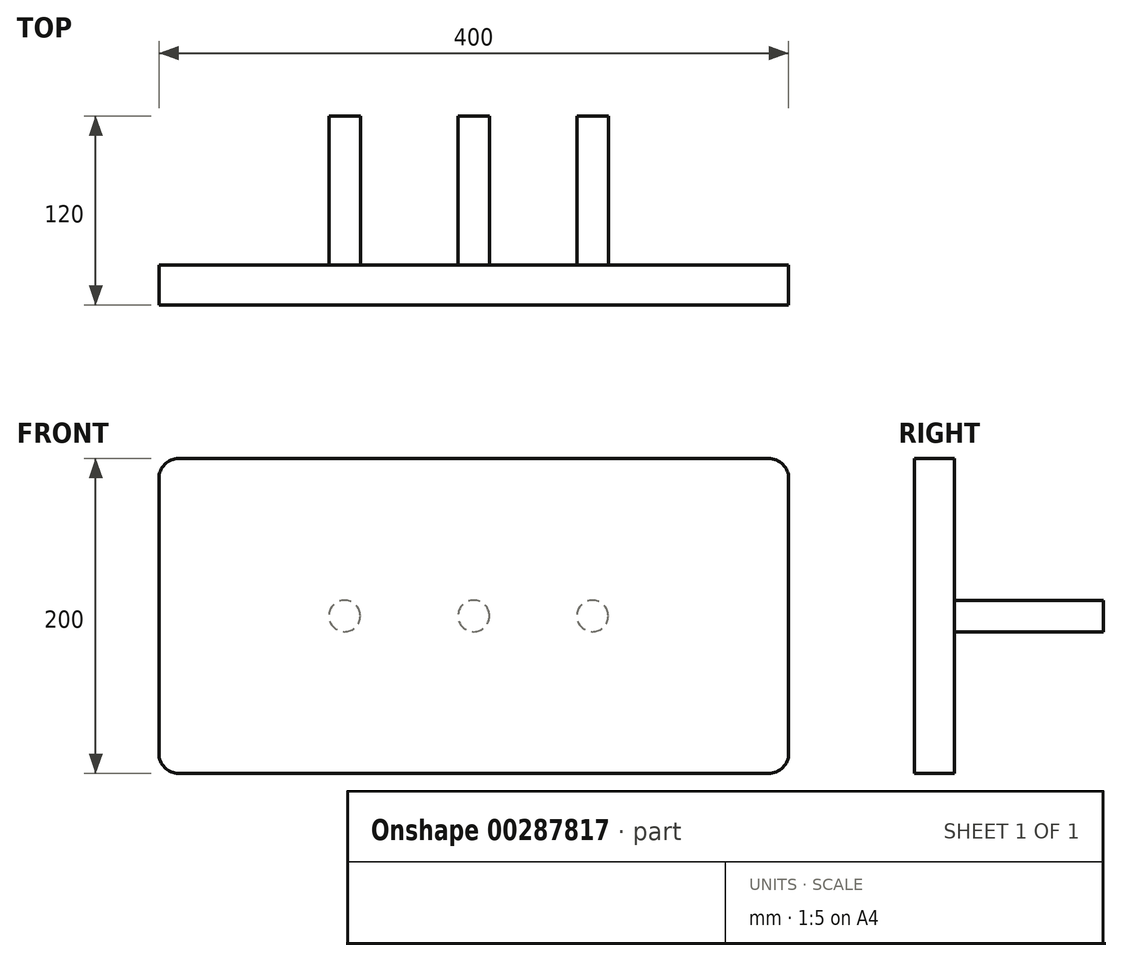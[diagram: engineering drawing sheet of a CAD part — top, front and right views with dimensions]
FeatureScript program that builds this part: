
annotation { "Feature Type Name" : "Feature", "Feature Type Description" : "" }
export const myFeature = defineFeature(function(context is Context, id is Id, definition is map)
    precondition{}
    {
        {
            var Q0;
            Q0=qCreatedBy(makeId("Front.planeOp"),FACE);
            var sketch = newSketch(context, id + "F0", { "sketchPlane" : qUnion([Q0])});
            skLineSegment(sketch, "E0.bottom", {"start": v(200, 100) * mm, "end": v(-200, 100) * mm});
            skLineSegment(sketch, "E0.top", {"start": v(200, -100) * mm, "end": v(-200, -100) * mm});
            skLineSegment(sketch, "E0.left", {"start": v(200, 100) * mm, "end": v(200, -100) * mm});
            skLineSegment(sketch, "E0.right", {"start": v(-200, 100) * mm, "end": v(-200, -100) * mm});
            skPoint(sketch, "E0.middle", {"position": v(0, 0) * mm});
            skSolve(sketch);
        }
        {
            var Q0;
            Q0=makeQuery(id+"F0.imprint","IMPRINT",FACE,{"disambiguationData":[TD([[makeQuery(id+"F0.imprint","IMPRINT",EDGE,{"derivedFrom":sQuery(id+"F0.wireOp",EDGE,"E0.bottom")}),1.0]])]});
            extrude(context, id + "F1", {"entities" : qUnion([Q0]), "depth" : 25.4 * mm});
        }
        {
            var Q0;
            Q0=makeQuery(id+"F1.opExtrude","CAP_FACE",FACE,{"disambiguationData":[OSD([sQuery(id+"F0.wireOp",EDGE,"E0.bottom"),sQuery(id+"F0.wireOp",EDGE,"E0.top"),sQuery(id+"F0.wireOp",EDGE,"E0.left"),sQuery(id+"F0.wireOp",EDGE,"E0.right")])],"isStart":false});
            var sketch = newSketch(context, id + "F2", { "sketchPlane" : qUnion([Q0])});
            skCircle(sketch, "E1", {"center": v(0, 0) * mm, "radius": 10 * mm});
            skCircle(sketch, "E2", {"center": v(-82.03, 0) * mm, "radius": 10 * mm});
            skCircle(sketch, "E3", {"center": v(75.47, 0) * mm, "radius": 10 * mm});
            skSolve(sketch);
        }
        {
            var Q0;
            Q0=makeQuery(id+"F1.opExtrude","SWEPT_EDGE",EDGE,{"disambiguationData":[OSD([sQuery(id+"F0.wireOp",EDGE,"E0.top"),sQuery(id+"F0.wireOp",EDGE,"E0.right")])]});
            var Q1;
            Q1=makeQuery(id+"F1.opExtrude","SWEPT_EDGE",EDGE,{"disambiguationData":[OSD([sQuery(id+"F0.wireOp",EDGE,"E0.top"),sQuery(id+"F0.wireOp",EDGE,"E0.left")])]});
            var Q2;
            Q2=makeQuery(id+"F1.opExtrude","SWEPT_EDGE",EDGE,{"disambiguationData":[OSD([sQuery(id+"F0.wireOp",EDGE,"E0.bottom"),sQuery(id+"F0.wireOp",EDGE,"E0.left")])]});
            fillet(context, id + "F3", {"entities" : qUnion([Q0, Q1, Q2]), "radius" : 12.7 * mm, "tangentPropagation" : true, "allowEdgeOverflow" : false});
        }
        {
            var Q0;
            Q0=makeQuery(id+"F1.opExtrude","SWEPT_EDGE",EDGE,{"disambiguationData":[OSD([sQuery(id+"F0.wireOp",EDGE,"E0.bottom"),sQuery(id+"F0.wireOp",EDGE,"E0.right")])]});
            fillet(context, id + "F4", {"entities" : qUnion([Q0]), "radius" : 12.7 * mm, "tangentPropagation" : true, "allowEdgeOverflow" : false});
        }
        {
            var Q0;
            Q0=makeQuery(id+"F2.imprint","IMPRINT",FACE,{"disambiguationData":[TD([[makeQuery(id+"F2.imprint","IMPRINT",EDGE,{"derivedFrom":sQuery(id+"F2.wireOp",EDGE,"E2")}),1.0]])]});
            var Q1;
            Q1=makeQuery(id+"F2.imprint","IMPRINT",FACE,{"disambiguationData":[TD([[makeQuery(id+"F2.imprint","IMPRINT",EDGE,{"derivedFrom":sQuery(id+"F2.wireOp",EDGE,"E1")}),1.0]])]});
            var Q2;
            Q2=makeQuery(id+"F2.imprint","IMPRINT",FACE,{"disambiguationData":[TD([[makeQuery(id+"F2.imprint","IMPRINT",EDGE,{"derivedFrom":sQuery(id+"F2.wireOp",EDGE,"E3")}),1.0]])]});
            extrude(context, id + "F5", {"entities" : qUnion([Q0, Q1, Q2]), "operationType" : NewBodyOperationType.ADD, "oppositeDirection" : true, "depth" : 120 * mm});
        }
    });
